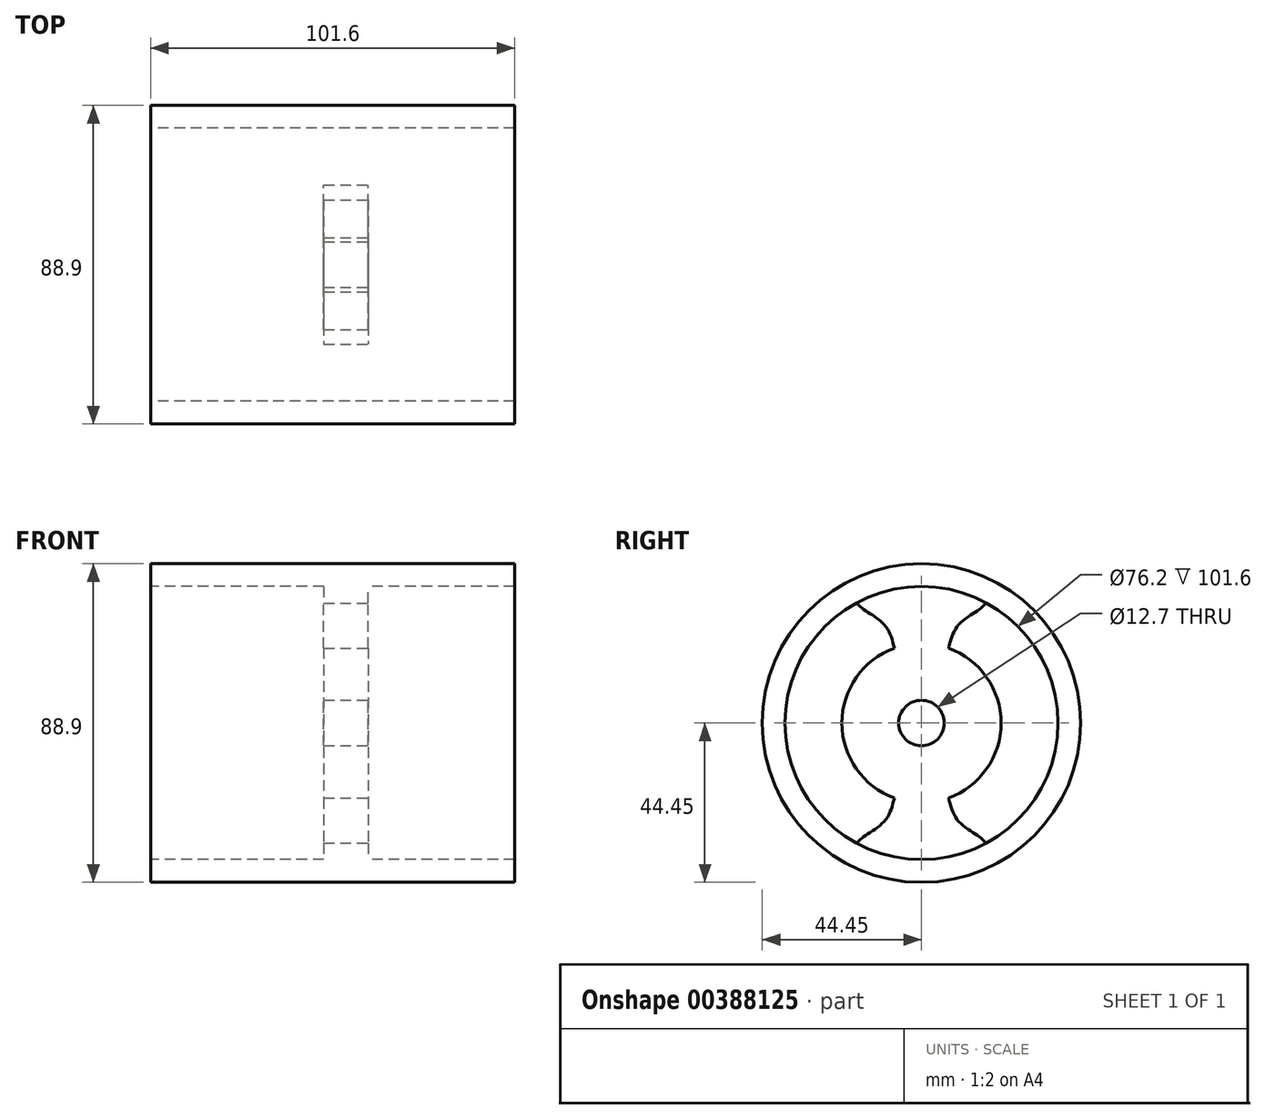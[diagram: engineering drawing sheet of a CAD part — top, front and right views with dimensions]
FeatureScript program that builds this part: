
annotation { "Feature Type Name" : "Feature", "Feature Type Description" : "" }
export const myFeature = defineFeature(function(context is Context, id is Id, definition is map)
    precondition{}
    {
        {
            var Q0;
            Q0=qCreatedBy(makeId("Front.planeOp"),FACE);
            var sketch = newSketch(context, id + "F0", { "sketchPlane" : qUnion([Q0])});
            skLineSegment(sketch, "E0.bottom", {"start": v(-60.75, 38.1) * mm, "end": v(40.85, 38.1) * mm});
            skLineSegment(sketch, "E0.top", {"start": v(-60.75, 44.45) * mm, "end": v(40.85, 44.45) * mm});
            skLineSegment(sketch, "E0.left", {"start": v(-60.75, 38.1) * mm, "end": v(-60.75, 44.45) * mm});
            skLineSegment(sketch, "E0.right", {"start": v(40.85, 38.1) * mm, "end": v(40.85, 44.45) * mm});
            skLineSegment(sketch, "E1", {"start": v(-75.5, 0) * mm, "end": v(1.8, 0) * mm, "construction": true});
            skLineSegment(sketch, "E2", {"start": v(-36.85, 0) * mm, "end": v(-39.65, 0) * mm, "construction": true});
            skSolve(sketch);
        }
        {
            var Q0;
            Q0 = qSketchRegion(id + "F0", true);
            var Q1;
            Q1=sQuery(id+"F0.wireOp",EDGE,"E1");
            revolve(context, id + "F1", {"entities" : qUnion([Q0]), "axis" : qUnion([Q1]), "revolveType" : RevolveType.FULL});
        }
        {
            var Q0;
            Q0=qCreatedBy(makeId("Right.planeOp"),FACE);
            var sketch = newSketch(context, id + "F2", { "sketchPlane" : qUnion([Q0])});
            skCircle(sketch, "E3", {"center": v(0, 0) * mm, "radius": 6.35 * mm});
            skCircle(sketch, "E4", {"center": v(0, 0) * mm, "radius": 22.23 * mm});
            skCircle(sketch, "E5.0", {"center": v(0, 0) * mm, "radius": 38.1 * mm});
            skFitSpline(sketch, "E6", {"points": [v(7.56, 20.9) * mm, v(10.18, 27.18) * mm, v(15.62, 31.37) * mm, v(18.12, 33.51) * mm], "startDerivative": vector(4.65, 18.22) * mm, "endDerivative": vector(8.19, 7.88) * mm});
            skFitSpline(sketch, "E7.MirrorCS", {"points": [v(-7.56, 20.9) * mm, v(-10.18, 27.18) * mm, v(-15.62, 31.37) * mm, v(-18.12, 33.51) * mm], "startDerivative": vector(-4.65, 18.22) * mm, "endDerivative": vector(-8.19, 7.88) * mm});
            skFitSpline(sketch, "E8.MirrorCS", {"points": [v(-7.56, -20.9) * mm, v(-10.18, -27.18) * mm, v(-15.62, -31.37) * mm, v(-18.12, -33.51) * mm], "startDerivative": vector(-4.65, -18.22) * mm, "endDerivative": vector(-8.19, -7.88) * mm});
            skFitSpline(sketch, "E9.MirrorCS", {"points": [v(7.56, -20.9) * mm, v(10.18, -27.18) * mm, v(15.62, -31.37) * mm, v(18.12, -33.51) * mm], "startDerivative": vector(4.65, -18.22) * mm, "endDerivative": vector(8.19, -7.88) * mm});
            skSolve(sketch);
        }
        {
            var Q0;
            {var subQ0=sQuery(id+"F2.wireOp",EDGE,"E6");Q0=makeQuery(id+"F2.imprint","IMPRINT",FACE,{"disambiguationData":[TD([[makeQuery(id+"F2.imprint","IMPRINT",EDGE,{"derivedFrom":subQ0}),1.0]])]});}
            var Q1;
            Q1=makeQuery(id+"F2.imprint","IMPRINT",FACE,{"disambiguationData":[TD([[makeQuery(id+"F2.imprint","IMPRINT",EDGE,{"derivedFrom":sQuery(id+"F2.wireOp",EDGE,"E3")}),-1.0]])]});
            var Q2;
            {var subQ0=sQuery(id+"F2.wireOp",EDGE,"E8.MirrorCS");Q2=makeQuery(id+"F2.imprint","IMPRINT",FACE,{"disambiguationData":[TD([[makeQuery(id+"F2.imprint","IMPRINT",EDGE,{"derivedFrom":subQ0}),1.0]])]});}
            extrude(context, id + "F3", {"entities" : qUnion([Q0, Q1, Q2]), "operationType" : NewBodyOperationType.ADD, "oppositeDirection" : true, "depth" : 12.45 * mm});
        }
    });
